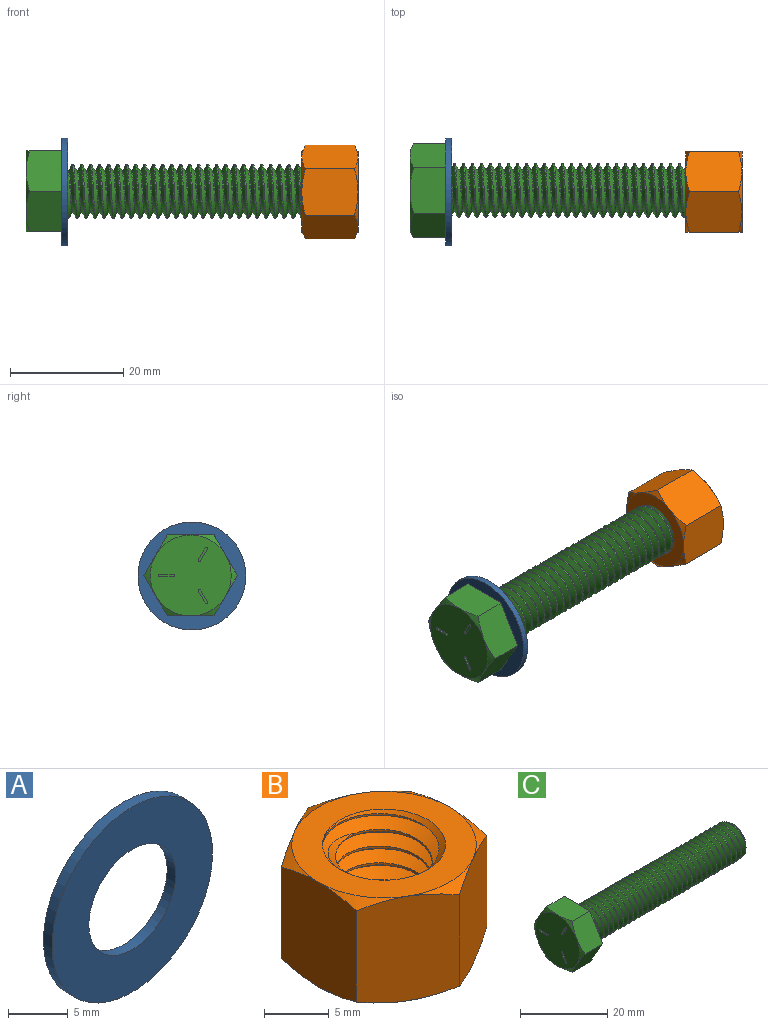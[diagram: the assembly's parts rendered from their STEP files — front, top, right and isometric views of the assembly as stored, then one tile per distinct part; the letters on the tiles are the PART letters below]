
ASSEMBLY  parts=3 mates=2
PART A: 4 faces, bbox 19.1x1x19.1 mm
  f0: cylinder r=9.53mm len=19.05mm, axis (0,-1,0), area 60.8mm2, adj f1,f2
  f1: plane 19.05x19.05mm, normal (0,1,0), area 201.5mm2, adj f0,f3
  f2: plane 19.05x19.05mm, normal (0,-1,0), area 201.5mm2, adj f0,f3
  f3: cylinder r=5.16mm len=10.31mm, axis (0,1,0), area 32.9mm2, adj f1,f2
PART B: 26 faces, bbox 17.2x17.2x11.8 mm
  f0: plane 14.29x14.29mm, normal (0,0,1), area 89.1mm2, adj f7,f12,f13,f14,f15,f16,f17,f18
  f1: plane 10.61x7.82mm, normal (-0.5,0.87,0), area 78.2mm2, adj f2,f6,f13,f18,f21,f22
  f2: plane 10.61x8.94mm, normal (-1,0,0), area 78.2mm2, adj f1,f3,f17,f18,f22,f23
  f3: plane 10.61x7.82mm, normal (-0.5,-0.87,0), area 78.2mm2, adj f2,f4,f16,f17,f23,f24
  f4: plane 10.61x7.82mm, normal (0.5,-0.87,0), area 78.2mm2, adj f3,f5,f15,f16,f24,f25
  f5: plane 10.61x8.94mm, normal (1,0,0), area 78.2mm2, adj f4,f6,f14,f15,f20,f25
  f6: plane 10.61x7.82mm, normal (0.5,0.87,0), area 78.2mm2, adj f1,f5,f13,f14,f20,f21
  f7: cylinder r=4.76mm len=9.92mm, axis (0,0,-1), area 37.2mm2, adj f0,f8,f9,f11
  f8: plane 14.29x14.29mm, normal (0,0,-1), area 89.1mm2, adj f7,f19,f20,f21,f22,f23,f24,f25
  f9: bspline ~10.72x9.53mm, area 179.1mm2, adj f7,f10,f12,f19
  f10: bspline ~8.33x7.46mm, area 22.8mm2, adj f9,f11,f12,f19
  f11: bspline ~10.52x9.53mm, area 177.8mm2, adj f7,f10,f12,f19
  f12: cone r=4.37mm half-angle=45deg, axis (0,0,1), area 20mm2, adj f0,f9,f10,f11
  f13: cone r=7.14mm half-angle=60deg, axis (0,0,-1), area 5mm2, adj f0,f1,f6
  f14: cone r=7.14mm half-angle=60deg, axis (0,0,-1), area 5mm2, adj f0,f5,f6
  f15: cone r=7.14mm half-angle=60deg, axis (0,0,-1), area 5mm2, adj f0,f4,f5
  f16: cone r=7.14mm half-angle=60deg, axis (0,0,-1), area 5mm2, adj f0,f3,f4
  f17: cone r=7.14mm half-angle=60deg, axis (0,0,-1), area 5mm2, adj f0,f2,f3
  f18: cone r=7.14mm half-angle=60deg, axis (0,0,-1), area 5mm2, adj f0,f1,f2
  f19: cone r=4.37mm half-angle=45deg, axis (0,0,-1), area 20mm2, adj f8,f9,f10,f11
  f20: cone r=7.14mm half-angle=60deg, axis (0,0,1), area 5mm2, adj f5,f6,f8
  f21: cone r=7.14mm half-angle=60deg, axis (0,0,1), area 5mm2, adj f1,f6,f8
  f22: cone r=7.14mm half-angle=60deg, axis (0,0,1), area 5mm2, adj f1,f2,f8
  f23: cone r=7.14mm half-angle=60deg, axis (0,0,1), area 5mm2, adj f2,f3,f8
  f24: cone r=7.14mm half-angle=60deg, axis (0,0,1), area 5mm2, adj f3,f4,f8
  f25: cone r=7.14mm half-angle=60deg, axis (0,0,1), area 5mm2, adj f4,f5,f8
PART C: 35 faces, bbox 58.6x17.2x17.2 mm
  f0: plane 8.94x7.03mm, normal (0,0,1), area 50.6mm2, adj f1,f5,f12,f13,f18
  f1: plane 7.82x7.03mm, normal (0,0.87,0.5), area 50.6mm2, adj f0,f2,f12,f17,f18
  f2: plane 7.82x7.03mm, normal (0,0.87,-0.5), area 50.6mm2, adj f1,f3,f12,f16,f17
  f3: plane 8.94x7.03mm, normal (0,0,-1), area 50.6mm2, adj f2,f4,f12,f15,f16
  f4: plane 7.82x7.03mm, normal (0,-0.87,-0.5), area 50.6mm2, adj f3,f5,f12,f14,f15
  f5: plane 7.82x7.03mm, normal (0,-0.87,0.5), area 50.6mm2, adj f0,f4,f12,f13,f14
  f6: cylinder r=4.76mm len=49.83mm, axis (1,0,0), area 187mm2, adj f8,f10,f11,f12
  f7: plane 7.6x7.57mm, normal (1,0,0), area 44.9mm2, adj f8,f9,f10,f11
  f8: cone r=3.79mm half-angle=45deg, axis (-1,0,0), area 17.1mm2, adj f6,f7,f10,f11
  f9: bspline ~51.4x7.46mm, area 149mm2, adj f7,f10,f11,f12
  f10: bspline ~51.59x9.53mm, area 1009.3mm2, adj f6,f7,f8,f9,f12
  f11: bspline ~52.19x9.53mm, area 1010.1mm2, adj f6,f7,f8,f9,f12
  f12: plane 16.52x14.31mm, normal (1,0,0), area 119.7mm2, adj f0,f1,f2,f3,f4,f5,f6,f9
  f13: cone r=7.14mm half-angle=60deg, axis (1,0,0), area 5mm2, adj f0,f5,f19
  f14: cone r=7.14mm half-angle=60deg, axis (1,0,0), area 5mm2, adj f4,f5,f19
  f15: cone r=7.14mm half-angle=60deg, axis (1,0,0), area 5mm2, adj f3,f4,f19
  f16: cone r=7.14mm half-angle=60deg, axis (1,0,0), area 5mm2, adj f2,f3,f19
  f17: cone r=7.14mm half-angle=60deg, axis (1,0,0), area 5mm2, adj f1,f2,f19
  f18: cone r=7.14mm half-angle=60deg, axis (1,0,0), area 5mm2, adj f0,f1,f19
  f19: plane 14.29x14.29mm, normal (-1,0,0), area 156.8mm2, adj f13,f14,f15,f16,f17,f18,f20,f21
  f20: cylinder r=0.21mm len=0.43mm, axis (-1,0,0), area 0.2mm2, adj f19,f21,f23,f24
  f21: plane 2.43x0.25mm, normal (0,0,-1), area 0.6mm2, adj f19,f20,f22,f24
  f22: cylinder r=0.21mm len=0.43mm, axis (-1,0,0), area 0.2mm2, adj f19,f21,f23,f24
  f23: plane 2.43x0.25mm, normal (0,0,1), area 0.6mm2, adj f19,f20,f22,f24
  f24: plane 2.86x0.43mm, normal (-1,0,0), area 1.2mm2, adj f20,f21,f22,f23
  f25: cylinder r=0.21mm len=0.4mm, axis (-1,0,0), area 0.2mm2, adj f19,f26,f28,f29
  f26: plane 2.1x1.21mm, normal (0,0.87,0.5), area 0.6mm2, adj f19,f25,f27,f29
  f27: cylinder r=0.21mm len=0.4mm, axis (-1,0,0), area 0.2mm2, adj f19,f26,f28,f29
  f28: plane 2.1x1.21mm, normal (0,-0.87,-0.5), area 0.6mm2, adj f19,f25,f27,f29
  f29: plane 2.53x1.64mm, normal (-1,0,0), area 1.2mm2, adj f25,f26,f27,f28
  f30: cylinder r=0.21mm len=0.4mm, axis (-1,0,0), area 0.2mm2, adj f19,f31,f33,f34
  f31: plane 2.1x1.21mm, normal (0,-0.87,0.5), area 0.6mm2, adj f19,f30,f32,f34
  f32: cylinder r=0.21mm len=0.4mm, axis (-1,0,0), area 0.2mm2, adj f19,f31,f33,f34
  f33: plane 2.1x1.21mm, normal (0,0.87,-0.5), area 0.6mm2, adj f19,f30,f32,f34
  f34: plane 2.53x1.64mm, normal (-1,0,0), area 1.2mm2, adj f30,f31,f32,f33
PLACE A rot(axis=(0.58,0.58,-0.58),120deg) t=(-28.56,-0.29,5.3)mm
PLACE B rot(axis=(0.58,-0.58,-0.58),120deg) t=(18.7,-0.29,5.3)mm
PLACE C t=(-6.33,-0.06,5.39)mm fixed
MATE fastened B.f12 <-> A.f0  axis (-1,0,0) through (13.74,-0.29,5.3)mm
MATE fastened A.f0 <-> C.f12  axis (-1,0,0) through (-28.56,-0.29,5.3)mm
